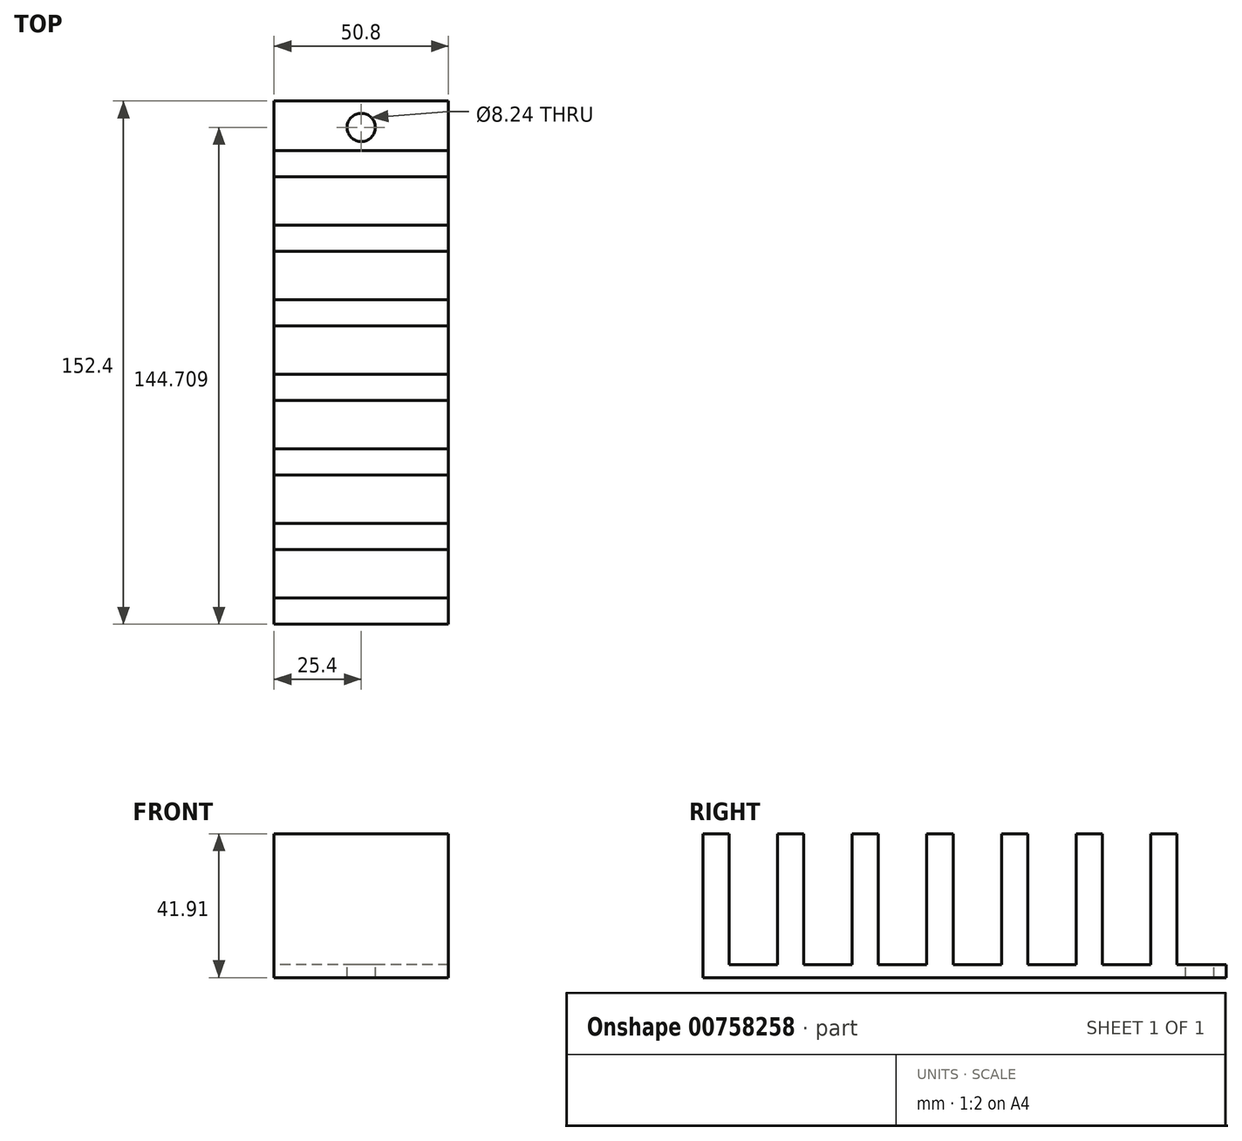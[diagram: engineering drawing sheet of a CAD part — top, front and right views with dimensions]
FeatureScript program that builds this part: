
annotation { "Feature Type Name" : "Feature", "Feature Type Description" : "" }
export const myFeature = defineFeature(function(context is Context, id is Id, definition is map)
    precondition{}
    {
        {
            var Q0;
            Q0=qCreatedBy(makeId("Top.planeOp"),FACE);
            var sketch = newSketch(context, id + "F0", { "sketchPlane" : qUnion([Q0])});
            skLineSegment(sketch, "E0.bottom", {"start": v(0, 0) * mm, "end": v(50.8, 0) * mm});
            skLineSegment(sketch, "E0.top", {"start": v(0, 152.4) * mm, "end": v(50.8, 152.4) * mm});
            skLineSegment(sketch, "E0.left", {"start": v(0, 0) * mm, "end": v(0, 152.4) * mm});
            skLineSegment(sketch, "E0.right", {"start": v(50.8, 0) * mm, "end": v(50.8, 152.4) * mm});
            skSolve(sketch);
        }
        {
            var Q0;
            Q0 = qSketchRegion(id + "F0", true);
            extrude(context, id + "F1", {"entities" : qUnion([Q0]), "depth" : 3.8 * mm, "offsetDistance" : 25.4 * mm});
        }
        {
            var Q0;
            Q0=makeQuery(id+"F1.opExtrude","CAP_FACE",FACE,{"disambiguationData":[OSD([sQuery(id+"F0.wireOp",EDGE,"E0.bottom"),sQuery(id+"F0.wireOp",EDGE,"E0.top"),sQuery(id+"F0.wireOp",EDGE,"E0.left"),sQuery(id+"F0.wireOp",EDGE,"E0.right")])],"isStart":false});
            var sketch = newSketch(context, id + "F2", { "sketchPlane" : qUnion([Q0])});
            skLineSegment(sketch, "E1.bottom", {"start": v(0, 0) * mm, "end": v(50.8, 0) * mm});
            skLineSegment(sketch, "E1.top", {"start": v(0, 7.62) * mm, "end": v(50.8, 7.62) * mm});
            skLineSegment(sketch, "E1.left", {"start": v(0, 0) * mm, "end": v(0, 7.62) * mm});
            skLineSegment(sketch, "E1.right", {"start": v(50.8, 0) * mm, "end": v(50.8, 7.62) * mm});
            skLineSegment(sketch, "E2.bottom", {"start": v(0, 21.72) * mm, "end": v(50.8, 21.72) * mm});
            skLineSegment(sketch, "E2.top", {"start": v(0, 29.34) * mm, "end": v(50.8, 29.34) * mm});
            skLineSegment(sketch, "E2.left", {"start": v(0, 21.72) * mm, "end": v(0, 29.34) * mm});
            skLineSegment(sketch, "E2.right", {"start": v(50.8, 21.72) * mm, "end": v(50.8, 29.34) * mm});
            skLineSegment(sketch, "E3.bottom", {"start": v(0, 43.44) * mm, "end": v(50.8, 43.44) * mm});
            skLineSegment(sketch, "E3.top", {"start": v(0, 51.06) * mm, "end": v(50.8, 51.06) * mm});
            skLineSegment(sketch, "E3.left", {"start": v(0, 43.44) * mm, "end": v(0, 51.06) * mm});
            skLineSegment(sketch, "E3.right", {"start": v(50.8, 43.44) * mm, "end": v(50.8, 51.06) * mm});
            skLineSegment(sketch, "E4", {"start": v(0, 65.16) * mm, "end": v(50.8, 65.16) * mm});
            skLineSegment(sketch, "E5", {"start": v(0, 65.16) * mm, "end": v(0, 72.78) * mm});
            skLineSegment(sketch, "E6", {"start": v(0, 72.78) * mm, "end": v(50.8, 72.78) * mm});
            skLineSegment(sketch, "E7", {"start": v(50.8, 72.78) * mm, "end": v(50.8, 65.16) * mm});
            skLineSegment(sketch, "E8", {"start": v(0, 72.78) * mm, "end": v(0, 65.16) * mm});
            skLineSegment(sketch, "E9", {"start": v(0, 86.88) * mm, "end": v(50.8, 86.88) * mm});
            skLineSegment(sketch, "E10", {"start": v(0, 86.88) * mm, "end": v(0, 94.5) * mm});
            skLineSegment(sketch, "E11", {"start": v(0, 94.5) * mm, "end": v(50.8, 94.5) * mm});
            skLineSegment(sketch, "E12", {"start": v(50.8, 94.5) * mm, "end": v(50.8, 86.88) * mm});
            skLineSegment(sketch, "E13", {"start": v(0, 108.6) * mm, "end": v(50.8, 108.6) * mm});
            skLineSegment(sketch, "E14", {"start": v(50.8, 108.6) * mm, "end": v(50.8, 116.22) * mm});
            skLineSegment(sketch, "E15", {"start": v(50.8, 116.22) * mm, "end": v(0, 116.22) * mm});
            skLineSegment(sketch, "E16", {"start": v(0, 116.22) * mm, "end": v(0, 108.6) * mm});
            skLineSegment(sketch, "E17", {"start": v(0, 130.32) * mm, "end": v(50.8, 130.32) * mm});
            skLineSegment(sketch, "E18", {"start": v(50.8, 130.32) * mm, "end": v(50.8, 137.94) * mm});
            skLineSegment(sketch, "E19", {"start": v(50.8, 137.94) * mm, "end": v(0, 137.94) * mm});
            skLineSegment(sketch, "E20", {"start": v(0, 137.94) * mm, "end": v(0, 130.32) * mm});
            skCircle(sketch, "E21", {"center": v(25.4, 147.35) * mm, "radius": 2.63 * mm});
            skPoint(sketch, "E21.centerSnap0", {"position": v(25.4, 152.4) * mm});
            skSolve(sketch);
        }
        {
            var Q0;
            Q0=makeQuery(id+"F2.imprint","IMPRINT",FACE,{"disambiguationData":[TD([[makeQuery(id+"F2.imprint","IMPRINT",EDGE,{"derivedFrom":sQuery(id+"F2.wireOp",EDGE,"E17")}),1.0]])]});
            var Q1;
            Q1=makeQuery(id+"F2.imprint","IMPRINT",FACE,{"disambiguationData":[TD([[makeQuery(id+"F2.imprint","IMPRINT",EDGE,{"derivedFrom":sQuery(id+"F2.wireOp",EDGE,"E13")}),1.0]])]});
            var Q2;
            Q2=makeQuery(id+"F2.imprint","IMPRINT",FACE,{"disambiguationData":[TD([[makeQuery(id+"F2.imprint","IMPRINT",EDGE,{"derivedFrom":sQuery(id+"F2.wireOp",EDGE,"E9")}),1.0]])]});
            var Q3;
            Q3=makeQuery(id+"F2.imprint","IMPRINT",FACE,{"disambiguationData":[TD([[makeQuery(id+"F2.imprint","IMPRINT",EDGE,{"derivedFrom":sQuery(id+"F2.wireOp",EDGE,"E4")}),1.0]])]});
            var Q4;
            Q4=makeQuery(id+"F2.imprint","IMPRINT",FACE,{"disambiguationData":[TD([[makeQuery(id+"F2.imprint","IMPRINT",EDGE,{"derivedFrom":sQuery(id+"F2.wireOp",EDGE,"E3.bottom")}),1.0]])]});
            var Q5;
            Q5=makeQuery(id+"F2.imprint","IMPRINT",FACE,{"disambiguationData":[TD([[makeQuery(id+"F2.imprint","IMPRINT",EDGE,{"derivedFrom":sQuery(id+"F2.wireOp",EDGE,"E1.bottom")}),1.0]])]});
            var Q6;
            Q6=makeQuery(id+"F2.imprint","IMPRINT",FACE,{"disambiguationData":[TD([[makeQuery(id+"F2.imprint","IMPRINT",EDGE,{"derivedFrom":sQuery(id+"F2.wireOp",EDGE,"E2.bottom")}),1.0]])]});
            extrude(context, id + "F3", {"entities" : qUnion([Q0, Q1, Q2, Q3, Q4, Q5, Q6]), "operationType" : NewBodyOperationType.ADD, "depth" : 38.1 * mm, "offsetDistance" : 25.4 * mm});
        }
        {
            var Q0;
            {var subQ0=sQuery(id+"F0.wireOp",EDGE,"E0.top");var subQ1=sQuery(id+"F0.wireOp",EDGE,"E0.left");var subQ2=sQuery(id+"F0.wireOp",EDGE,"E0.right");Q0=makeQuery(id+"F3.boolean.opBoolean","SPLIT",FACE,{"disambiguationData":[TD([makeQuery(id+"F1.opExtrude","SWEPT_FACE",FACE,{"disambiguationData":[OSD([subQ0])]})])],"derivedFrom":makeQuery(id+"F1.opExtrude","CAP_FACE",FACE,{"disambiguationData":[OSD([sQuery(id+"F0.wireOp",EDGE,"E0.bottom"),subQ0,subQ1,subQ2])],"isStart":false})});}
            var sketch = newSketch(context, id + "F4", { "sketchPlane" : qUnion([Q0])});
            skCircle(sketch, "E22", {"center": v(25.4, 144.7) * mm, "radius": 4.12 * mm});
            skPoint(sketch, "E22.centerSnap0", {"position": v(25.4, 152.4) * mm});
            skSolve(sketch);
        }
        {
            var Q0;
            Q0 = qSketchRegion(id + "F4", true);
            extrude(context, id + "F5", {"entities" : qUnion([Q0]), "operationType" : NewBodyOperationType.REMOVE, "oppositeDirection" : true, "depth" : 25.4 * mm, "offsetDistance" : 25.4 * mm});
        }
    });
